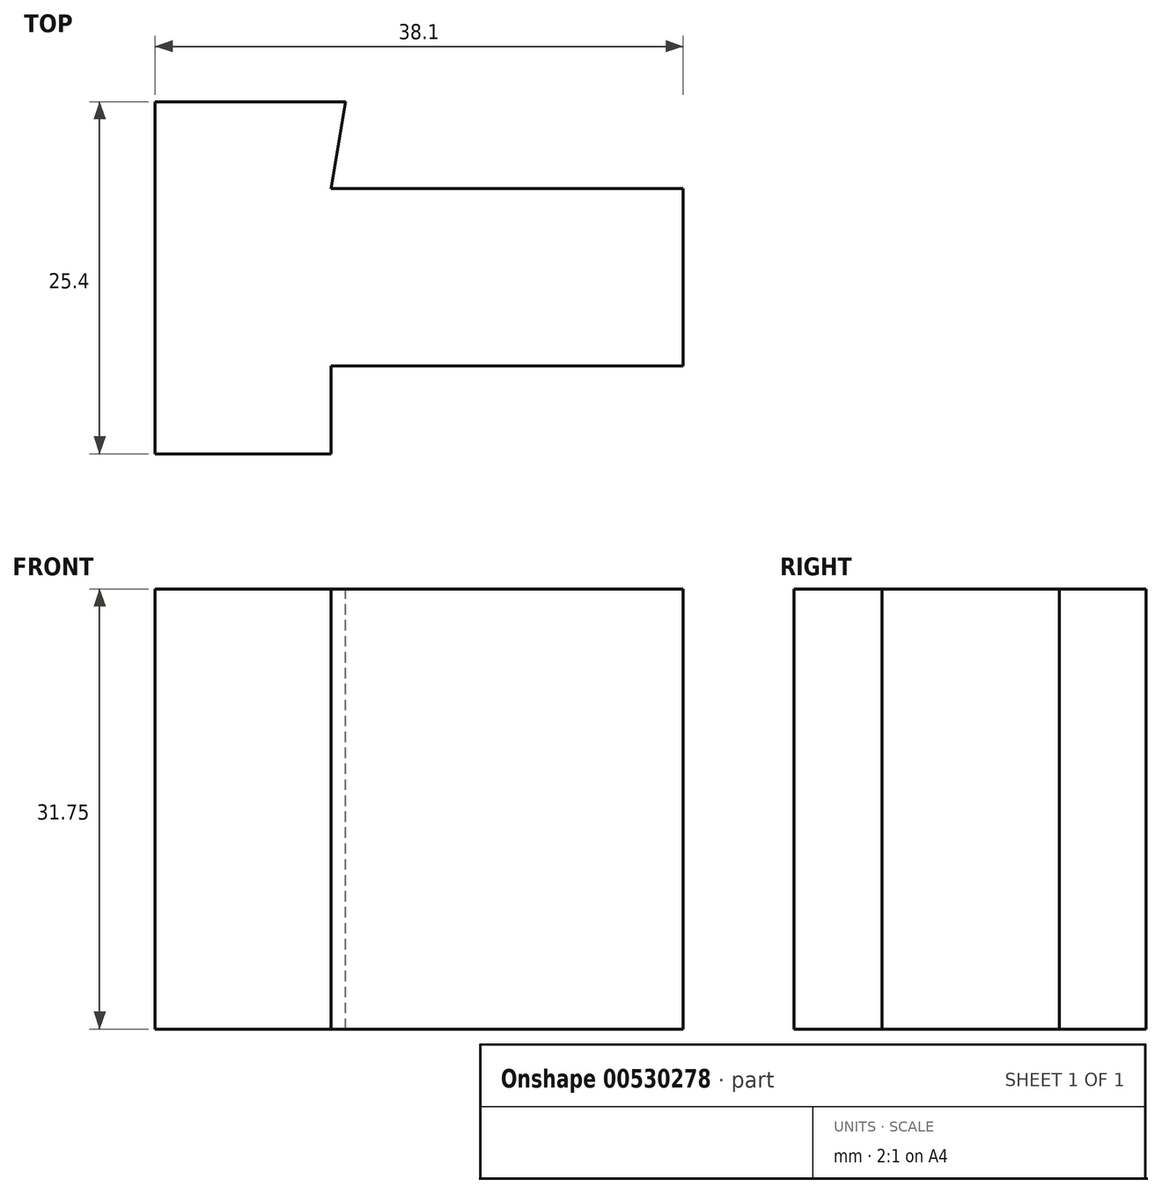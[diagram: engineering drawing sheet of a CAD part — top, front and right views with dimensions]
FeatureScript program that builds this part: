
annotation { "Feature Type Name" : "Feature", "Feature Type Description" : "" }
export const myFeature = defineFeature(function(context is Context, id is Id, definition is map)
    precondition{}
    {
        {
            var Q0;
            Q0=qCreatedBy(makeId("Front.planeOp"),FACE);
            var sketch = newSketch(context, id + "F0", { "sketchPlane" : qUnion([Q0])});
            skLineSegment(sketch, "E0", {"start": v(-59.8, 31.75) * mm, "end": v(-59.8, 0) * mm});
            skLineSegment(sketch, "E1", {"start": v(-59.8, 0) * mm, "end": v(-21.7, 0) * mm});
            skLineSegment(sketch, "E2", {"start": v(-21.7, 0) * mm, "end": v(-21.7, 31.75) * mm});
            skLineSegment(sketch, "E3", {"start": v(-21.7, 31.75) * mm, "end": v(-59.8, 31.75) * mm});
            skSolve(sketch);
        }
        {
            var Q0;
            Q0 = qSketchRegion(id + "F0", true);
            extrude(context, id + "F1", {"entities" : qUnion([Q0]), "depth" : 25.4 * mm, "offsetDistance" : 25.4 * mm});
        }
        {
            var Q0;
            Q0=makeQuery(id+"F1.opExtrude","SWEPT_FACE",FACE,{"disambiguationData":[OSD([sQuery(id+"F0.wireOp",EDGE,"E3")])]});
            var sketch = newSketch(context, id + "F2", { "sketchPlane" : qUnion([Q0])});
            skLineSegment(sketch, "E4", {"start": v(-21.7, -19.05) * mm, "end": v(-47.1, -19.05) * mm});
            skLineSegment(sketch, "E5", {"start": v(-21.7, -6.35) * mm, "end": v(-47.1, -6.35) * mm});
            skLineSegment(sketch, "E6", {"start": v(-47.1, -6.35) * mm, "end": v(-47.1, 0) * mm});
            skLineSegment(sketch, "E7", {"start": v(-47.1, -19.05) * mm, "end": v(-47.1, -25.4) * mm});
            skSolve(sketch);
        }
        {
            var Q0;
            Q0 = qSketchRegion(id + "F2", true);
            var Q1;
            {var subQ0=sQuery(id+"F2.wireOp",EDGE,"E4");Q1=makeQuery(id+"F2.imprint","IMPRINT",FACE,{"disambiguationData":[TD([[makeQuery(id+"F2.imprint","IMPRINT",EDGE,{"derivedFrom":subQ0}),1.0]])]});}
            extrude(context, id + "F3", {"entities" : qUnion([Q0, Q1]), "operationType" : NewBodyOperationType.REMOVE, "oppositeDirection" : true, "depth" : 25.4 * mm, "offsetDistance" : 25.4 * mm});
        }
        {
            var Q0;
            Q0=makeQuery(id+"F3.boolean.opBoolean","COPY",FACE,{"derivedFrom":makeQuery(id+"F3.opExtrude","CAP_FACE",FACE,{"disambiguationData":[OSD([sQuery(id+"F0.wireOp",EDGE,"E2"),sQuery(id+"F0.wireOp",EDGE,"E3"),sQuery(id+"F2.wireOp",EDGE,"E4"),sQuery(id+"F2.wireOp",EDGE,"E7")])],"isStart":false})});
            extrude(context, id + "F4", {"entities" : qUnion([Q0]), "operationType" : NewBodyOperationType.REMOVE, "oppositeDirection" : true, "depth" : 6.35 * mm, "offsetDistance" : 25.4 * mm});
        }
        {
            var Q0;
            Q0=makeQuery(id+"F1.opExtrude","SWEPT_FACE",FACE,{"disambiguationData":[OSD([sQuery(id+"F0.wireOp",EDGE,"E3")])]});
            var sketch = newSketch(context, id + "F5", { "sketchPlane" : qUnion([Q0])});
            skLineSegment(sketch, "E8", {"start": v(-21.7, -6.27) * mm, "end": v(-47.1, -6.27) * mm});
            skLineSegment(sketch, "E9", {"start": v(-46.08, 0) * mm, "end": v(-47.1, -6.27) * mm});
            skSolve(sketch);
        }
        {
            var Q0;
            {var subQ0=sQuery(id+"F5.wireOp",EDGE,"E8");Q0=makeQuery(id+"F5.imprint","IMPRINT",FACE,{"disambiguationData":[TD([[makeQuery(id+"F5.imprint","IMPRINT",EDGE,{"derivedFrom":subQ0}),-1.0]])]});}
            extrude(context, id + "F6", {"entities" : qUnion([Q0]), "operationType" : NewBodyOperationType.ADD, "depth" : 31.75 * mm, "offsetDistance" : 25.4 * mm});
        }
        {
            var Q0;
            Q0=makeQuery(id+"F6.opExtrude","CAP_FACE",FACE,{"disambiguationData":[OSD([sQuery(id+"F0.wireOp",EDGE,"E2"),sQuery(id+"F0.wireOp",EDGE,"E3"),sQuery(id+"F5.wireOp",EDGE,"E8"),sQuery(id+"F5.wireOp",EDGE,"E9")])],"isStart":false});
            extrude(context, id + "F7", {"entities" : qUnion([Q0]), "operationType" : NewBodyOperationType.REMOVE, "oppositeDirection" : true, "depth" : 57.15 * mm, "offsetDistance" : 25.4 * mm});
        }
        {
            var Q0;
            Q0=makeQuery(id+"F7.boolean.opBoolean","COPY",FACE,{"derivedFrom":makeQuery(id+"F7.opExtrude","CAP_FACE",FACE,{"disambiguationData":[OSD([sQuery(id+"F0.wireOp",EDGE,"E2"),sQuery(id+"F0.wireOp",EDGE,"E3"),sQuery(id+"F5.wireOp",EDGE,"E8"),sQuery(id+"F5.wireOp",EDGE,"E9")])],"isStart":false})});
            extrude(context, id + "F8", {"entities" : qUnion([Q0]), "operationType" : NewBodyOperationType.REMOVE, "oppositeDirection" : true, "depth" : 25.4 * mm, "offsetDistance" : 25.4 * mm});
        }
    });
